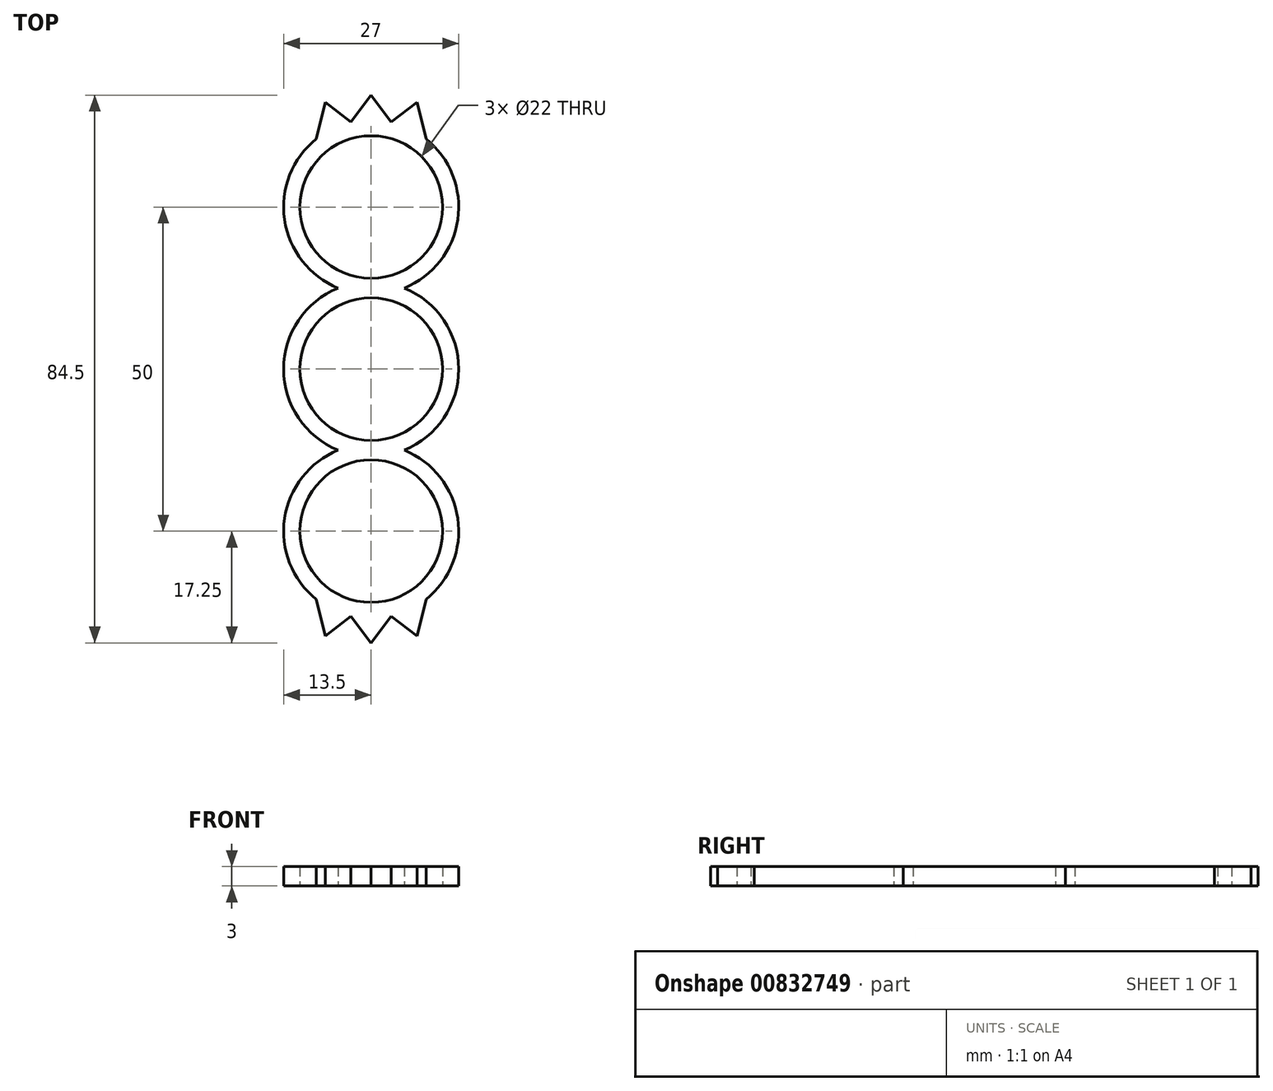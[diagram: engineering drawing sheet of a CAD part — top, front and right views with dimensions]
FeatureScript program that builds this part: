
annotation { "Feature Type Name" : "Feature", "Feature Type Description" : "" }
export const myFeature = defineFeature(function(context is Context, id is Id, definition is map)
    precondition{}
    {
        {
            var Q0;
            Q0=qCreatedBy(makeId("Top.planeOp"),FACE);
            var sketch = newSketch(context, id + "F0", { "sketchPlane" : qUnion([Q0])});
            skCircle(sketch, "E0", {"center": v(0, 0) * mm, "radius": 11 * mm});
            skArc(sketch, "E1", {"start": v(5.1, -12.5) * mm, "mid": v(13.5, 0) * mm, "end": v(5.1, 12.5) * mm});
            skCircle(sketch, "E2", {"center": v(0, 25) * mm, "radius": 11 * mm});
            skArc(sketch, "E3", {"start": v(5.1, 12.5) * mm, "mid": v(13.36, 23.05) * mm, "end": v(8.46, 35.52) * mm});
            skArc(sketch, "E4.MirrorC", {"start": v(5.1, 12.5) * mm, "mid": v(13.5, 0) * mm, "end": v(5.1, -12.5) * mm});
            skArc(sketch, "E5.MirrorC", {"start": v(5.1, -12.5) * mm, "mid": v(13.36, -23.05) * mm, "end": v(8.46, -35.52) * mm});
            skCircle(sketch, "E6.MirrorC", {"center": v(0, -25) * mm, "radius": 11 * mm});
            skArc(sketch, "E7.trimOffspring", {"start": v(-5.1, 12.5) * mm, "mid": v(-13.5, 0) * mm, "end": v(-5.1, -12.5) * mm});
            skArc(sketch, "E8.trimOffspring", {"start": v(-5.1, -12.5) * mm, "mid": v(-13.5, 0) * mm, "end": v(-5.1, 12.5) * mm});
            skLineSegment(sketch, "E9", {"start": v(0, 42.25) * mm, "end": v(-3.1, 38.14) * mm});
            skLineSegment(sketch, "E10.MirrorCS", {"start": v(0, 42.25) * mm, "end": v(3.1, 38.14) * mm});
            skLineSegment(sketch, "E11", {"start": v(-3.1, 38.14) * mm, "end": v(-7.1, 41.15) * mm});
            skLineSegment(sketch, "E12", {"start": v(-7.1, 41.15) * mm, "end": v(-8.46, 35.52) * mm});
            skLineSegment(sketch, "E13.MirrorCS", {"start": v(3.1, 38.14) * mm, "end": v(7.1, 41.15) * mm});
            skLineSegment(sketch, "E14.MirrorCS", {"start": v(7.1, 41.15) * mm, "end": v(8.46, 35.52) * mm});
            skLineSegment(sketch, "E15.MirrorCS", {"start": v(-7.1, -41.15) * mm, "end": v(-8.46, -35.52) * mm});
            skLineSegment(sketch, "E16.MirrorCS", {"start": v(-3.1, -38.14) * mm, "end": v(-7.1, -41.15) * mm});
            skLineSegment(sketch, "E17.MirrorCS", {"start": v(0, -42.25) * mm, "end": v(-3.1, -38.14) * mm});
            skLineSegment(sketch, "E18.MirrorCS", {"start": v(0, -42.25) * mm, "end": v(3.1, -38.14) * mm});
            skLineSegment(sketch, "E19.MirrorCS", {"start": v(3.1, -38.14) * mm, "end": v(7.1, -41.15) * mm});
            skLineSegment(sketch, "E20.MirrorCS", {"start": v(7.1, -41.15) * mm, "end": v(8.46, -35.52) * mm});
            skArc(sketch, "E21.trimOffspring", {"start": v(-8.46, 35.52) * mm, "mid": v(-13.36, 23.05) * mm, "end": v(-5.1, 12.5) * mm});
            skArc(sketch, "E22.trimOffspring", {"start": v(-8.46, -35.52) * mm, "mid": v(-13.36, -23.05) * mm, "end": v(-5.1, -12.5) * mm});
            skSolve(sketch);
        }
        {
            var Q0;
            Q0 = qSketchRegion(id + "F0", true);
            extrude(context, id + "F1", {"entities" : qUnion([Q0]), "depth" : 3 * mm, "offsetDistance" : 25 * mm});
        }
    });
